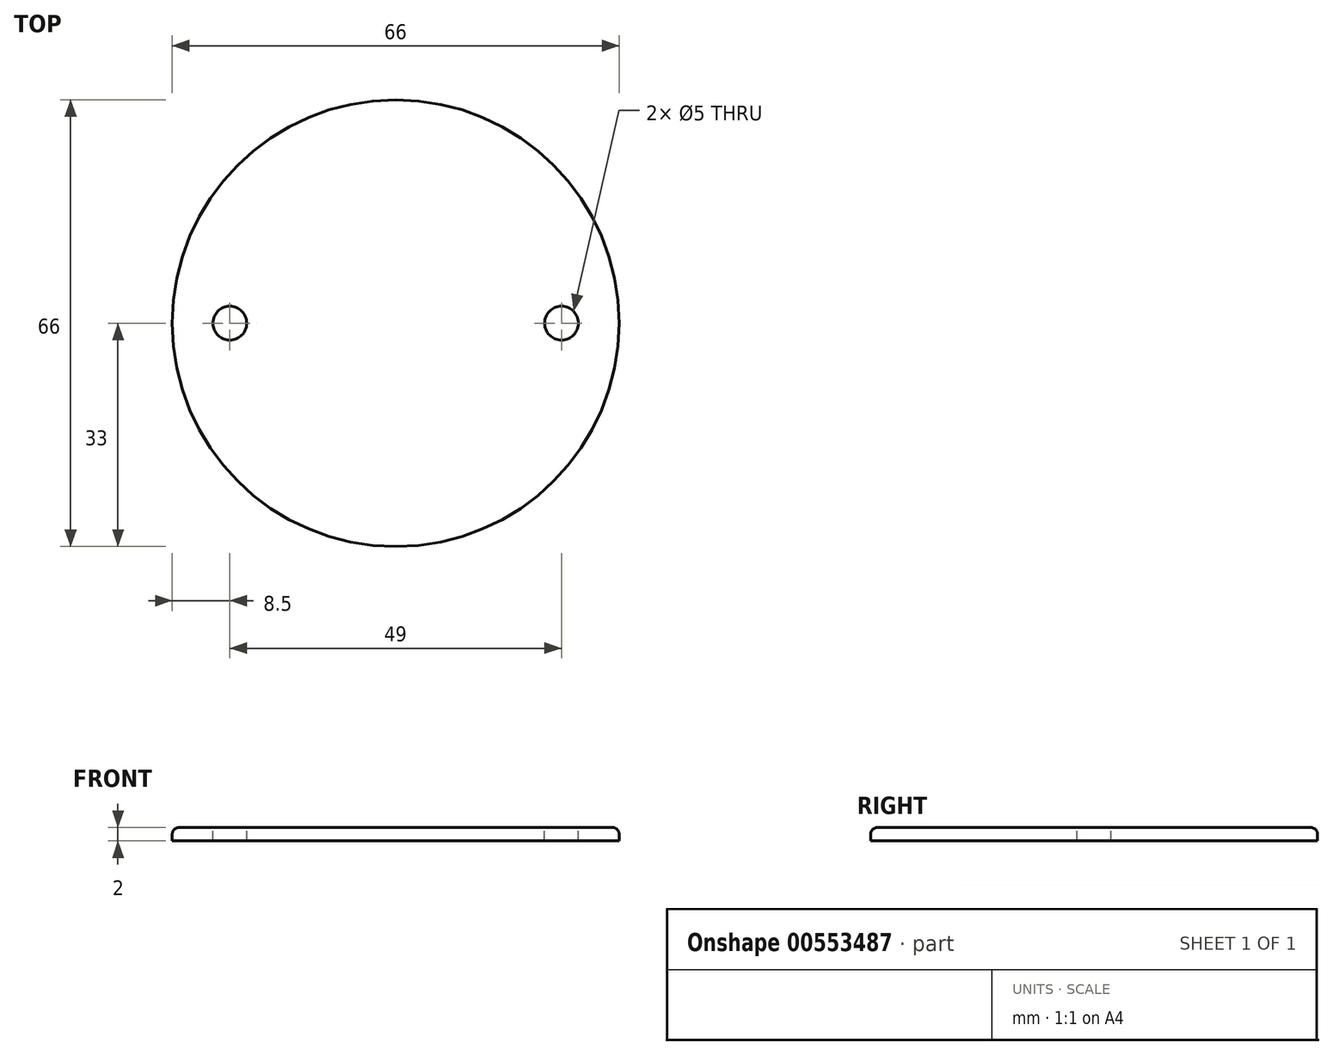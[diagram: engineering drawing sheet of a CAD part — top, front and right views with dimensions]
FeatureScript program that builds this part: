
annotation { "Feature Type Name" : "Feature", "Feature Type Description" : "" }
export const myFeature = defineFeature(function(context is Context, id is Id, definition is map)
    precondition{}
    {
        {
            var Q0;
            Q0=qCreatedBy(makeId("Top.planeOp"),FACE);
            var sketch = newSketch(context, id + "F0", { "sketchPlane" : qUnion([Q0])});
            skCircle(sketch, "E0", {"center": v(0, 0) * mm, "radius": 33 * mm});
            skSolve(sketch);
        }
        {
            var Q0;
            Q0=makeQuery(id+"F0.imprint","IMPRINT",FACE,{"disambiguationData":[TD([[makeQuery(id+"F0.imprint","IMPRINT",EDGE,{"derivedFrom":sQuery(id+"F0.wireOp",EDGE,"E0")}),1.0]])]});
            extrude(context, id + "F1", {"entities" : qUnion([Q0]), "depth" : 2 * mm, "offsetDistance" : 25 * mm});
        }
        {
            var Q0;
            Q0=makeQuery(id+"F1.opExtrude","CAP_FACE",FACE,{"disambiguationData":[OSD([sQuery(id+"F0.wireOp",EDGE,"E0")])],"isStart":false});
            var sketch = newSketch(context, id + "F2", { "sketchPlane" : qUnion([Q0])});
            skLineSegment(sketch, "E1", {"start": v(0, 33) * mm, "end": v(0, -33) * mm, "construction": true});
            skLineSegment(sketch, "E2", {"start": v(-33, 0) * mm, "end": v(33, 0) * mm, "construction": true});
            skCircle(sketch, "E3", {"center": v(24.5, 0) * mm, "radius": 2.5 * mm});
            skCircle(sketch, "E4", {"center": v(-24.5, 0) * mm, "radius": 2.5 * mm});
            skSolve(sketch);
        }
        {
            var Q0;
            Q0=makeQuery(id+"F2.imprint","IMPRINT",FACE,{"disambiguationData":[TD([[makeQuery(id+"F2.imprint","IMPRINT",EDGE,{"derivedFrom":sQuery(id+"F2.wireOp",EDGE,"E4")}),1.0]])]});
            var Q1;
            Q1=makeQuery(id+"F2.imprint","IMPRINT",FACE,{"disambiguationData":[TD([[makeQuery(id+"F2.imprint","IMPRINT",EDGE,{"derivedFrom":sQuery(id+"F2.wireOp",EDGE,"E3")}),1.0]])]});
            var Q2;
            Q2=sQuery(id+"F2.wireOp",EDGE,"E4");
            var Q3;
            Q3=sQuery(id+"F2.wireOp",EDGE,"E3");
            extrude(context, id + "F3", {"entities" : qUnion([Q0, Q1]), "operationType" : NewBodyOperationType.REMOVE, "surfaceEntities" : qUnion([Q2, Q3]), "oppositeDirection" : true, "depth" : 25 * mm, "offsetDistance" : 25 * mm});
        }
        {
            var Q0;
            Q0=makeQuery(id+"F1.opExtrude","CAP_EDGE",EDGE,{"disambiguationData":[OSD([sQuery(id+"F0.wireOp",EDGE,"E0")])],"isStart":false});
            fillet(context, id + "F4", {"entities" : qUnion([Q0]), "radius" : 1 * mm, "tangentPropagation" : true, "allowEdgeOverflow" : false});
        }
    });
